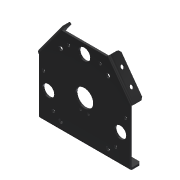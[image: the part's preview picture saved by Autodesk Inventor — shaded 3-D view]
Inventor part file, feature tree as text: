
AUTODESK INVENTOR PART (.ipt)
format: ipt  version: 2013 (Build 170138000, 138)  size: 140,800 bytes
history: native  units: in
note: dims shown in document units (in); Inventor stores cm internally (conversion verified against a paired STEP export)
features: chamfer x1, other x1, imported_body x1
ambient origin geometry x8: Origin, YZ Plane, XZ Plane, XY Plane, X Axis, Y Axis, Z Axis, Center Point
feature tree (3):
  chamfer  "Chamfer1"  [1 undecoded]
  other  "217-2752-001 Rev11"
  imported_body  "Base1"
note: 1 required parameter value undecoded (feature->parameter linkage not recoverable at this tier; creation-order binding heuristic only, values carry confidence <= 0.55)
